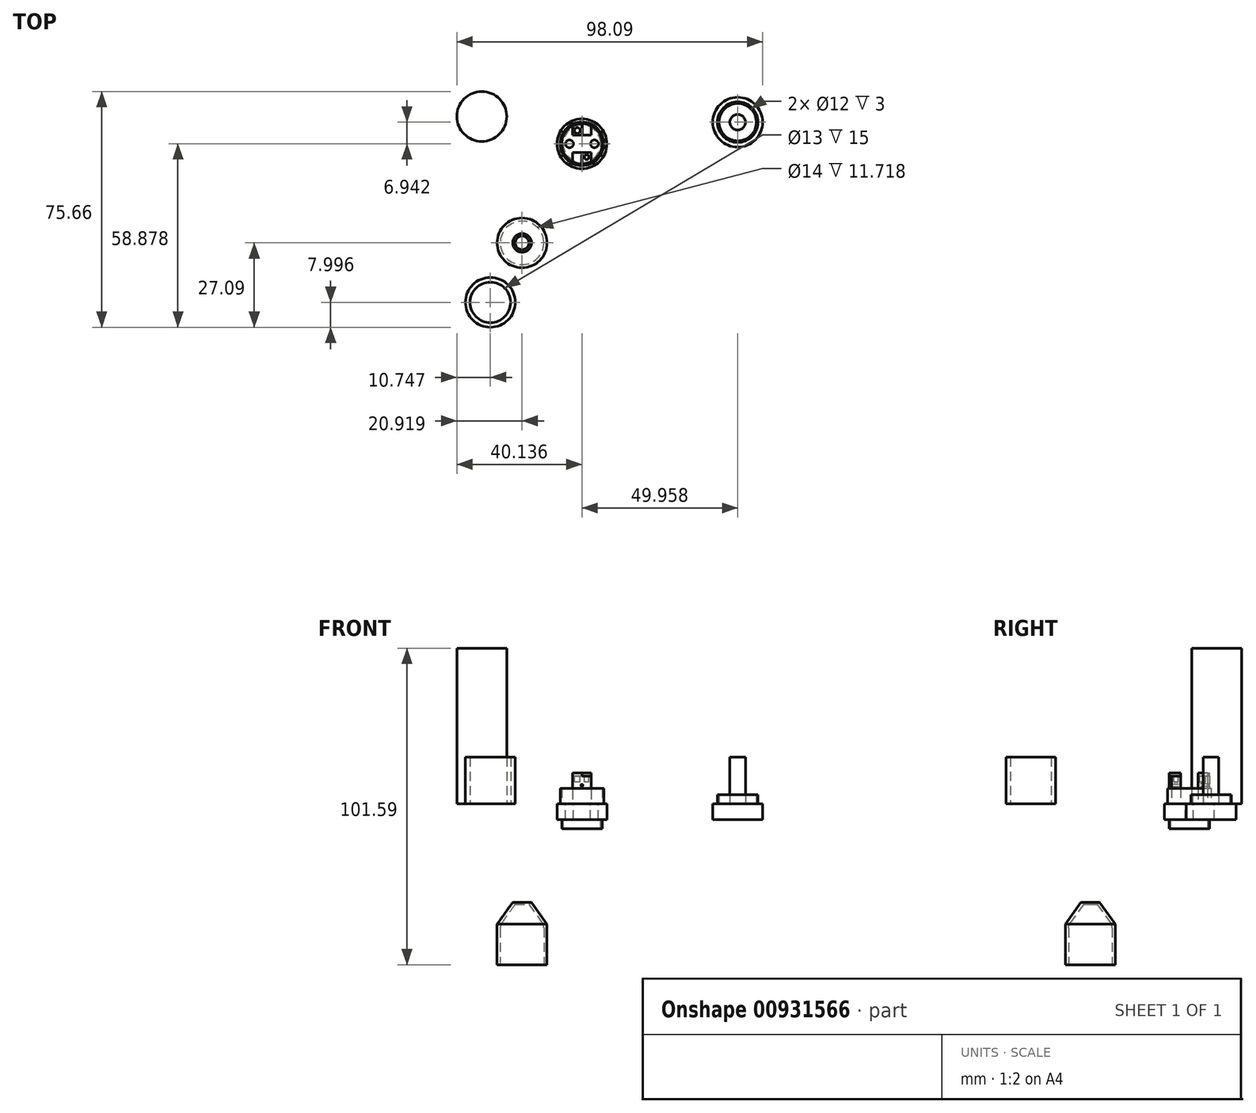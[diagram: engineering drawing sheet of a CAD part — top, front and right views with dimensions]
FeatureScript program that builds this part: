
annotation { "Feature Type Name" : "Feature", "Feature Type Description" : "" }
export const myFeature = defineFeature(function(context is Context, id is Id, definition is map)
    precondition{}
    {
        {
            var Q0;
            Q0=qCreatedBy(makeId("Top.planeOp"),FACE);
            var sketch = newSketch(context, id + "F0", { "sketchPlane" : qUnion([Q0])});
            skCircle(sketch, "E0", {"center": v(-50.1, 40.57) * mm, "radius": 8 * mm});
            skSolve(sketch);
        }
        {
            var Q0;
            Q0=makeQuery(id+"F0.imprint","IMPRINT",FACE,{"disambiguationData":[TD([[makeQuery(id+"F0.imprint","IMPRINT",EDGE,{"derivedFrom":sQuery(id+"F0.wireOp",EDGE,"E0")}),1.0]])]});
            extrude(context, id + "F1", {"entities" : qUnion([Q0]), "depth" : 50 * mm, "offsetDistance" : 25 * mm});
        }
        {
            var Q0;
            Q0=qCreatedBy(makeId("Top.planeOp"),FACE);
            var sketch = newSketch(context, id + "F2", { "sketchPlane" : qUnion([Q0])});
            skCircle(sketch, "E1", {"center": v(-17.96, 31.79) * mm, "radius": 8 * mm});
            skCircle(sketch, "E2.0", {"center": v(-17.96, 31.79) * mm, "radius": 6.5 * mm});
            skCircle(sketch, "E3.0", {"center": v(-17.96, 31.79) * mm, "radius": 7 * mm});
            skCircle(sketch, "E4.0", {"center": v(-17.96, 31.79) * mm, "radius": 6 * mm});
            skLineSegment(sketch, "E5.left", {"start": v(-20.96, 37.55) * mm, "end": v(-20.96, 34.55) * mm});
            skLineSegment(sketch, "E5.right", {"start": v(-14.96, 37.55) * mm, "end": v(-14.96, 34.55) * mm});
            skLineSegment(sketch, "E6", {"start": v(-20.96, 29.02) * mm, "end": v(-14.96, 29.02) * mm});
            skLineSegment(sketch, "E7", {"start": v(-20.96, 34.55) * mm, "end": v(-14.96, 34.55) * mm});
            skLineSegment(sketch, "E8.trimOffspring", {"start": v(-20.96, 29.02) * mm, "end": v(-20.96, 26.02) * mm});
            skLineSegment(sketch, "E9.trimOffspring", {"start": v(-14.96, 29.02) * mm, "end": v(-14.96, 26.02) * mm});
            skPoint(sketch, "E10", {"position": v(-13.96, 31.79) * mm});
            skPoint(sketch, "E11", {"position": v(-21.96, 31.79) * mm});
            skSolve(sketch);
        }
        {
            var Q0;
            Q0=qCreatedBy(makeId("Top.planeOp"),FACE);
            var sketch = newSketch(context, id + "F3", { "sketchPlane" : qUnion([Q0])});
            skCircle(sketch, "E12", {"center": v(32, 38.73) * mm, "radius": 8 * mm});
            skCircle(sketch, "E13.0", {"center": v(32, 38.73) * mm, "radius": 6.5 * mm});
            skCircle(sketch, "E14", {"center": v(32, 38.73) * mm, "radius": 2.5 * mm});
            skCircle(sketch, "E15.0", {"center": v(32, 38.73) * mm, "radius": 6 * mm});
            skPoint(sketch, "E16", {"position": v(-21.96, 31.79) * mm});
            skPoint(sketch, "E17", {"position": v(-13.96, 31.79) * mm});
            skSolve(sketch);
        }
        {
            var Q0;
            Q0=makeQuery(id+"F3.imprint","IMPRINT",FACE,{"disambiguationData":[TD([[makeQuery(id+"F3.imprint","IMPRINT",EDGE,{"derivedFrom":sQuery(id+"F3.wireOp",EDGE,"E14")}),1.0]])]});
            var Q1;
            Q1=makeQuery(id+"F3.imprint","IMPRINT",FACE,{"disambiguationData":[TD([[makeQuery(id+"F3.imprint","IMPRINT",EDGE,{"derivedFrom":sQuery(id+"F3.wireOp",EDGE,"E14")}),-1.0]])]});
            var Q2;
            Q2=makeQuery(id+"F3.imprint","IMPRINT",FACE,{"disambiguationData":[TD([[makeQuery(id+"F3.imprint","IMPRINT",EDGE,{"derivedFrom":sQuery(id+"F3.wireOp",EDGE,"E13.0")}),1.0]])]});
            var Q3;
            Q3=makeQuery(id+"F3.imprint","IMPRINT",FACE,{"disambiguationData":[TD([[makeQuery(id+"F3.imprint","IMPRINT",EDGE,{"derivedFrom":sQuery(id+"F3.wireOp",EDGE,"E12")}),1.0]])]});
            extrude(context, id + "F4", {"entities" : qUnion([Q0, Q1, Q2, Q3]), "oppositeDirection" : true, "depth" : 5 * mm, "offsetDistance" : 25 * mm});
        }
        {
            var Q0;
            Q0=makeQuery(id+"F3.imprint","IMPRINT",FACE,{"disambiguationData":[TD([[makeQuery(id+"F3.imprint","IMPRINT",EDGE,{"derivedFrom":sQuery(id+"F3.wireOp",EDGE,"E13.0")}),1.0]])]});
            extrude(context, id + "F5", {"entities" : qUnion([Q0]), "operationType" : NewBodyOperationType.ADD, "depth" : 3 * mm, "offsetDistance" : 25 * mm});
        }
        {
            var Q0;
            Q0=makeQuery(id+"F3.imprint","IMPRINT",FACE,{"disambiguationData":[TD([[makeQuery(id+"F3.imprint","IMPRINT",EDGE,{"derivedFrom":sQuery(id+"F3.wireOp",EDGE,"E14")}),1.0]])]});
            extrude(context, id + "F6", {"entities" : qUnion([Q0]), "operationType" : NewBodyOperationType.ADD, "depth" : 15 * mm, "offsetDistance" : 25 * mm});
        }
        {
            var Q0;
            {var subQ0=sQuery(id+"F2.wireOp",EDGE,"E8.trimOffspring");var subQ1=sQuery(id+"F2.wireOp",EDGE,"E2.0");var subQ2=makeQuery(id+"F2.imprint","INTERSECT",VERTEX,{"derivedFrom":[subQ1,subQ0]});Q0=makeQuery(id+"F2.imprint","IMPRINT",FACE,{"disambiguationData":[TD([[makeQuery(id+"F2.imprint","IMPRINT",EDGE,{"disambiguationData":[TD([[subQ2,-1.0]])],"derivedFrom":subQ1}),1.0]])]});}
            var Q1;
            {var subQ0=sQuery(id+"F2.wireOp",EDGE,"E5.left");var subQ1=sQuery(id+"F2.wireOp",EDGE,"E2.0");var subQ2=makeQuery(id+"F2.imprint","INTERSECT",VERTEX,{"derivedFrom":[subQ1,subQ0]});Q1=makeQuery(id+"F2.imprint","IMPRINT",FACE,{"disambiguationData":[TD([[makeQuery(id+"F2.imprint","IMPRINT",EDGE,{"disambiguationData":[TD([[subQ2,-1.0]])],"derivedFrom":subQ1}),1.0]])]});}
            var Q2;
            Q2=makeQuery(id+"F2.imprint","IMPRINT",FACE,{"disambiguationData":[TD([[makeQuery(id+"F2.imprint","IMPRINT",EDGE,{"derivedFrom":sQuery(id+"F2.wireOp",EDGE,"E1")}),1.0]])]});
            var Q3;
            {var subQ5=sQuery(id+"F2.wireOp",EDGE,"E7");Q3=makeQuery(id+"F2.imprint","IMPRINT",FACE,{"disambiguationData":[TD([[makeQuery(id+"F2.imprint","IMPRINT",EDGE,{"derivedFrom":subQ5}),1.0]])]});}
            var Q4;
            Q4=makeQuery(id+"F2.imprint","IMPRINT",FACE,{"disambiguationData":[TD([[makeQuery(id+"F2.imprint","IMPRINT",EDGE,{"derivedFrom":sQuery(id+"F2.wireOp",EDGE,"E3.0")}),1.0]])]});
            var Q5;
            {var subQ0=sQuery(id+"F2.wireOp",EDGE,"E5.right");var subQ1=sQuery(id+"F2.wireOp",EDGE,"E2.0");var subQ2=makeQuery(id+"F2.imprint","INTERSECT",VERTEX,{"derivedFrom":[subQ1,subQ0]});Q5=makeQuery(id+"F2.imprint","IMPRINT",FACE,{"disambiguationData":[TD([[makeQuery(id+"F2.imprint","IMPRINT",EDGE,{"disambiguationData":[TD([[subQ2,1.0]])],"derivedFrom":subQ1}),1.0]])]});}
            var Q6;
            {var subQ5=sQuery(id+"F2.wireOp",EDGE,"E6");Q6=makeQuery(id+"F2.imprint","IMPRINT",FACE,{"disambiguationData":[TD([[makeQuery(id+"F2.imprint","IMPRINT",EDGE,{"derivedFrom":subQ5}),-1.0]])]});}
            var Q7;
            {var subQ10=sQuery(id+"F2.wireOp",EDGE,"E6");Q7=makeQuery(id+"F2.imprint","IMPRINT",FACE,{"disambiguationData":[TD([[makeQuery(id+"F2.imprint","IMPRINT",EDGE,{"derivedFrom":subQ10}),1.0]])]});}
            var Q8;
            {var subQ0=sQuery(id+"F2.wireOp",EDGE,"E5.left");var subQ1=sQuery(id+"F2.wireOp",EDGE,"E2.0");var subQ2=makeQuery(id+"F2.imprint","INTERSECT",VERTEX,{"derivedFrom":[subQ1,subQ0]});Q8=makeQuery(id+"F2.imprint","IMPRINT",FACE,{"disambiguationData":[TD([[makeQuery(id+"F2.imprint","IMPRINT",EDGE,{"disambiguationData":[TD([[subQ2,1.0]])],"derivedFrom":subQ1}),1.0]])]});}
            extrude(context, id + "F7", {"entities" : qUnion([Q0, Q1, Q2, Q3, Q4, Q5, Q6, Q7, Q8]), "oppositeDirection" : true, "depth" : 5 * mm, "offsetDistance" : 25 * mm});
        }
        {
            var Q0;
            {var subQ0=sQuery(id+"F2.wireOp",EDGE,"E5.right");var subQ1=sQuery(id+"F2.wireOp",EDGE,"E2.0");var subQ2=makeQuery(id+"F2.imprint","INTERSECT",VERTEX,{"derivedFrom":[subQ1,subQ0]});Q0=makeQuery(id+"F2.imprint","IMPRINT",FACE,{"disambiguationData":[TD([[makeQuery(id+"F2.imprint","IMPRINT",EDGE,{"disambiguationData":[TD([[subQ2,1.0]])],"derivedFrom":subQ1}),1.0]])]});}
            var Q1;
            {var subQ0=sQuery(id+"F2.wireOp",EDGE,"E8.trimOffspring");var subQ1=sQuery(id+"F2.wireOp",EDGE,"E2.0");var subQ2=makeQuery(id+"F2.imprint","INTERSECT",VERTEX,{"derivedFrom":[subQ1,subQ0]});Q1=makeQuery(id+"F2.imprint","IMPRINT",FACE,{"disambiguationData":[TD([[makeQuery(id+"F2.imprint","IMPRINT",EDGE,{"disambiguationData":[TD([[subQ2,-1.0]])],"derivedFrom":subQ1}),1.0]])]});}
            var Q2;
            {var subQ0=sQuery(id+"F2.wireOp",EDGE,"E5.left");var subQ1=sQuery(id+"F2.wireOp",EDGE,"E2.0");var subQ2=makeQuery(id+"F2.imprint","INTERSECT",VERTEX,{"derivedFrom":[subQ1,subQ0]});Q2=makeQuery(id+"F2.imprint","IMPRINT",FACE,{"disambiguationData":[TD([[makeQuery(id+"F2.imprint","IMPRINT",EDGE,{"disambiguationData":[TD([[subQ2,1.0]])],"derivedFrom":subQ1}),1.0]])]});}
            var Q3;
            {var subQ0=sQuery(id+"F2.wireOp",EDGE,"E5.left");var subQ1=sQuery(id+"F2.wireOp",EDGE,"E2.0");var subQ2=makeQuery(id+"F2.imprint","INTERSECT",VERTEX,{"derivedFrom":[subQ1,subQ0]});Q3=makeQuery(id+"F2.imprint","IMPRINT",FACE,{"disambiguationData":[TD([[makeQuery(id+"F2.imprint","IMPRINT",EDGE,{"disambiguationData":[TD([[subQ2,-1.0]])],"derivedFrom":subQ1}),1.0]])]});}
            extrude(context, id + "F8", {"entities" : qUnion([Q0, Q1, Q2, Q3]), "operationType" : NewBodyOperationType.ADD, "oppositeDirection" : true, "depth" : 8 * mm, "offsetDistance" : 25 * mm});
        }
        {
            var Q0;
            Q0=makeQuery(id+"F2.imprint","IMPRINT",FACE,{"disambiguationData":[TD([[makeQuery(id+"F2.imprint","IMPRINT",EDGE,{"derivedFrom":sQuery(id+"F2.wireOp",EDGE,"E3.0")}),1.0]])]});
            extrude(context, id + "F9", {"entities" : qUnion([Q0]), "operationType" : NewBodyOperationType.ADD, "depth" : 5 * mm, "offsetDistance" : 25 * mm});
        }
        {
            var Q0;
            {var subQ10=sQuery(id+"F2.wireOp",EDGE,"E6");Q0=makeQuery(id+"F2.imprint","IMPRINT",FACE,{"disambiguationData":[TD([[makeQuery(id+"F2.imprint","IMPRINT",EDGE,{"derivedFrom":subQ10}),1.0]])]});}
            var sketch = newSketch(context, id + "F10", { "sketchPlane" : qUnion([Q0])});
            skPoint(sketch, "E18", {"position": v(-13.96, 31.79) * mm});
            skPoint(sketch, "E19", {"position": v(-21.96, 31.79) * mm});
            skCircle(sketch, "E20", {"center": v(-21.96, 31.79) * mm, "radius": 1.25 * mm});
            skCircle(sketch, "E21", {"center": v(-13.96, 31.79) * mm, "radius": 1.25 * mm});
            skSolve(sketch);
        }
        {
            var Q0;
            Q0=makeQuery(id+"F10.imprint","IMPRINT",FACE,{"disambiguationData":[TD([[makeQuery(id+"F10.imprint","IMPRINT",EDGE,{"derivedFrom":sQuery(id+"F10.wireOp",EDGE,"E21")}),1.0]])]});
            var Q1;
            Q1=makeQuery(id+"F10.imprint","IMPRINT",FACE,{"disambiguationData":[TD([[makeQuery(id+"F10.imprint","IMPRINT",EDGE,{"derivedFrom":sQuery(id+"F10.wireOp",EDGE,"E20")}),1.0]])]});
            extrude(context, id + "F11", {"entities" : qUnion([Q0, Q1]), "operationType" : NewBodyOperationType.REMOVE, "oppositeDirection" : true, "depth" : 40 * mm, "offsetDistance" : 25 * mm});
        }
        {
            var Q0;
            {var subQ5=sQuery(id+"F2.wireOp",EDGE,"E6");Q0=makeQuery(id+"F2.imprint","IMPRINT",FACE,{"disambiguationData":[TD([[makeQuery(id+"F2.imprint","IMPRINT",EDGE,{"derivedFrom":subQ5}),-1.0]])]});}
            var Q1;
            {var subQ0=sQuery(id+"F2.wireOp",EDGE,"E8.trimOffspring");var subQ1=sQuery(id+"F2.wireOp",EDGE,"E2.0");var subQ2=makeQuery(id+"F2.imprint","INTERSECT",VERTEX,{"derivedFrom":[subQ1,subQ0]});Q1=makeQuery(id+"F2.imprint","IMPRINT",FACE,{"disambiguationData":[TD([[makeQuery(id+"F2.imprint","IMPRINT",EDGE,{"disambiguationData":[TD([[subQ2,-1.0]])],"derivedFrom":subQ1}),1.0]])]});}
            var Q2;
            {var subQ0=sQuery(id+"F2.wireOp",EDGE,"E5.left");var subQ1=sQuery(id+"F2.wireOp",EDGE,"E2.0");var subQ2=makeQuery(id+"F2.imprint","INTERSECT",VERTEX,{"derivedFrom":[subQ1,subQ0]});Q2=makeQuery(id+"F2.imprint","IMPRINT",FACE,{"disambiguationData":[TD([[makeQuery(id+"F2.imprint","IMPRINT",EDGE,{"disambiguationData":[TD([[subQ2,1.0]])],"derivedFrom":subQ1}),1.0]])]});}
            var Q3;
            {var subQ5=sQuery(id+"F2.wireOp",EDGE,"E7");Q3=makeQuery(id+"F2.imprint","IMPRINT",FACE,{"disambiguationData":[TD([[makeQuery(id+"F2.imprint","IMPRINT",EDGE,{"derivedFrom":subQ5}),1.0]])]});}
            extrude(context, id + "F12", {"entities" : qUnion([Q0, Q1, Q2, Q3]), "operationType" : NewBodyOperationType.ADD, "depth" : 10 * mm, "offsetDistance" : 25 * mm});
        }
        {
            var Q0;
            Q0=makeQuery(id+"F12.opExtrude","SWEPT_FACE",FACE,{"disambiguationData":[OSD([sQuery(id+"F2.wireOp",EDGE,"E7")])]});
            var sketch = newSketch(context, id + "F13", { "sketchPlane" : qUnion([Q0])});
            skPoint(sketch, "E22", {"position": v(-17.96, 6) * mm});
            skCircle(sketch, "E23", {"center": v(-17.96, 6) * mm, "radius": 0.35 * mm});
            skSolve(sketch);
        }
        {
            var Q0;
            Q0=makeQuery(id+"F12.opExtrude","SWEPT_FACE",FACE,{"disambiguationData":[OSD([sQuery(id+"F2.wireOp",EDGE,"E6")])]});
            var sketch = newSketch(context, id + "F14", { "sketchPlane" : qUnion([Q0])});
            skPoint(sketch, "E24", {"position": v(17.96, 6) * mm});
            skCircle(sketch, "E25", {"center": v(17.96, 6) * mm, "radius": 0.35 * mm});
            skSolve(sketch);
        }
        {
            var Q0;
            Q0=makeQuery(id+"F13.imprint","IMPRINT",FACE,{"disambiguationData":[TD([[makeQuery(id+"F13.imprint","IMPRINT",EDGE,{"derivedFrom":sQuery(id+"F13.wireOp",EDGE,"E23")}),1.0]])]});
            extrude(context, id + "F15", {"entities" : qUnion([Q0]), "operationType" : NewBodyOperationType.REMOVE, "oppositeDirection" : true, "depth" : 25 * mm, "offsetDistance" : 25 * mm});
        }
        {
            var Q0;
            Q0=makeQuery(id+"F14.imprint","IMPRINT",FACE,{"disambiguationData":[TD([[makeQuery(id+"F14.imprint","IMPRINT",EDGE,{"derivedFrom":sQuery(id+"F14.wireOp",EDGE,"E25")}),1.0]])]});
            extrude(context, id + "F16", {"entities" : qUnion([Q0]), "operationType" : NewBodyOperationType.REMOVE, "oppositeDirection" : true, "depth" : 25 * mm, "offsetDistance" : 25 * mm});
        }
        {
            var Q0;
            Q0=qCreatedBy(makeId("Top.planeOp"),FACE);
            var sketch = newSketch(context, id + "F17", { "sketchPlane" : qUnion([Q0])});
            skCircle(sketch, "E26", {"center": v(-47.35, -19.1) * mm, "radius": 8 * mm});
            skCircle(sketch, "E27.0", {"center": v(-47.35, -19.1) * mm, "radius": 6.5 * mm});
            skSolve(sketch);
        }
        {
            var Q0;
            Q0=makeQuery(id+"F17.imprint","IMPRINT",FACE,{"disambiguationData":[TD([[makeQuery(id+"F17.imprint","IMPRINT",EDGE,{"derivedFrom":sQuery(id+"F17.wireOp",EDGE,"E26")}),1.0]])]});
            extrude(context, id + "F18", {"entities" : qUnion([Q0]), "depth" : 15 * mm, "offsetDistance" : 25 * mm});
        }
        {
            var Q0;
            Q0=qCreatedBy(makeId("Front.planeOp"),FACE);
            var sketch = newSketch(context, id + "F19", { "sketchPlane" : qUnion([Q0])});
            skLineSegment(sketch, "E28.top", {"start": v(-45.18, -51.59) * mm, "end": v(-44.18, -51.59) * mm});
            skLineSegment(sketch, "E28.left", {"start": v(-45.18, -38.59) * mm, "end": v(-45.18, -51.59) * mm});
            skLineSegment(sketch, "E29", {"start": v(-45.18, -51.59) * mm, "end": v(-45.18, -38.59) * mm});
            skLineSegment(sketch, "E30", {"start": v(-45.18, -38.59) * mm, "end": v(-40.18, -31.59) * mm});
            skLineSegment(sketch, "E31.0", {"start": v(-44.18, -38.9) * mm, "end": v(-39.37, -32.17) * mm});
            skLineSegment(sketch, "E31.1", {"start": v(-44.18, -51.59) * mm, "end": v(-44.18, -38.9) * mm});
            skLineSegment(sketch, "E32", {"start": v(-40.18, -31.59) * mm, "end": v(-39.37, -32.17) * mm});
            skLineSegment(sketch, "E33", {"start": v(-37.18, -61.59) * mm, "end": v(-37.18, -31.59) * mm});
            skSolve(sketch);
        }
        {
            var Q0;
            Q0=makeQuery(id+"F19.imprint","IMPRINT",FACE,{"disambiguationData":[TD([[makeQuery(id+"F19.imprint","IMPRINT",EDGE,{"derivedFrom":sQuery(id+"F19.wireOp",EDGE,"E28.top")}),1.0]])]});
            var Q1;
            Q1=sQuery(id+"F19.wireOp",EDGE,"E33");
            revolve(context, id + "F20", {"surfaceOperationType" : NewSurfaceOperationType.NEW, "entities" : qUnion([Q0]), "axis" : qUnion([Q1]), "revolveType" : RevolveType.FULL});
        }
        {
            var Q0;
            Q0=makeQuery(id+"F20.opRevolve","SWEPT_EDGE",EDGE,{"disambiguationData":[OSD([sQuery(id+"F19.wireOp",EDGE,"E31.0"),sQuery(id+"F19.wireOp",EDGE,"E31.1")])]});
            fillet(context, id + "F21", {"entities" : qUnion([Q0]), "radius" : 3 * mm, "tangentPropagation" : true, "allowEdgeOverflow" : false});
        }
        {
            var Q0;
            Q0=makeQuery(id+"F12.opExtrude","CAP_FACE",FACE,{"disambiguationData":[OSD([sQuery(id+"F2.wireOp",EDGE,"E2.0"),sQuery(id+"F2.wireOp",EDGE,"E5.left"),sQuery(id+"F2.wireOp",EDGE,"E5.right"),sQuery(id+"F2.wireOp",EDGE,"E7")])],"isStart":false});
            var sketch = newSketch(context, id + "F22", { "sketchPlane" : qUnion([Q0])});
            skLineSegment(sketch, "E34.bottom", {"start": v(-20.96, 34.55) * mm, "end": v(-17.96, 34.55) * mm});
            skLineSegment(sketch, "E34.top", {"start": v(-20.96, 37.55) * mm, "end": v(-17.96, 37.55) * mm});
            skLineSegment(sketch, "E34.left", {"start": v(-20.96, 34.55) * mm, "end": v(-20.96, 37.55) * mm});
            skLineSegment(sketch, "E34.right", {"start": v(-17.96, 34.55) * mm, "end": v(-17.96, 37.55) * mm});
            skPoint(sketch, "E35", {"position": v(-19.46, 36.05) * mm});
            skCircle(sketch, "E36", {"center": v(-19.46, 36.05) * mm, "radius": 0.92 * mm});
            skSolve(sketch);
        }
        {
            var Q0;
            Q0=makeQuery(id+"F22.imprint","IMPRINT",FACE,{"disambiguationData":[TD([[makeQuery(id+"F22.imprint","IMPRINT",EDGE,{"derivedFrom":sQuery(id+"F22.wireOp",EDGE,"E36")}),1.0]])]});
            var Q1;
            Q1=makeQuery(id+"F22.imprint","IMPRINT",FACE,{"disambiguationData":[TD([[makeQuery(id+"F22.imprint","IMPRINT",EDGE,{"derivedFrom":sQuery(id+"F22.wireOp",EDGE,"E34.bottom")}),1.0]])]});
            extrude(context, id + "F23", {"entities" : qUnion([Q0, Q1]), "operationType" : NewBodyOperationType.REMOVE, "oppositeDirection" : true, "depth" : 1 * mm, "offsetDistance" : 25 * mm});
        }
        {
            var Q0;
            Q0=makeQuery(id+"F22.imprint","IMPRINT",FACE,{"disambiguationData":[TD([[makeQuery(id+"F22.imprint","IMPRINT",EDGE,{"derivedFrom":sQuery(id+"F22.wireOp",EDGE,"E36")}),1.0]])]});
            extrude(context, id + "F24", {"entities" : qUnion([Q0]), "operationType" : NewBodyOperationType.REMOVE, "oppositeDirection" : true, "depth" : 3 * mm, "offsetDistance" : 25 * mm});
        }
        {
            var Q0;
            Q0=makeQuery(id+"F12.opExtrude","CAP_FACE",FACE,{"disambiguationData":[OSD([sQuery(id+"F2.wireOp",EDGE,"E2.0"),sQuery(id+"F2.wireOp",EDGE,"E6"),sQuery(id+"F2.wireOp",EDGE,"E8.trimOffspring"),sQuery(id+"F2.wireOp",EDGE,"E9.trimOffspring")])],"isStart":false});
            var sketch = newSketch(context, id + "F25", { "sketchPlane" : qUnion([Q0])});
            skLineSegment(sketch, "E37.bottom", {"start": v(-14.96, 29.02) * mm, "end": v(-17.96, 29.02) * mm});
            skLineSegment(sketch, "E37.top", {"start": v(-14.96, 26.02) * mm, "end": v(-17.96, 26.02) * mm});
            skLineSegment(sketch, "E37.left", {"start": v(-14.96, 29.02) * mm, "end": v(-14.96, 26.02) * mm});
            skLineSegment(sketch, "E37.right", {"start": v(-17.96, 29.02) * mm, "end": v(-17.96, 26.02) * mm});
            skPoint(sketch, "E38", {"position": v(-16.46, 27.52) * mm});
            skPoint(sketch, "E38.positionSnap0", {"position": v(-16.46, 29.02) * mm});
            skCircle(sketch, "E39", {"center": v(-16.46, 27.52) * mm, "radius": 0.75 * mm});
            skSolve(sketch);
        }
        {
            var Q0;
            Q0=makeQuery(id+"F25.imprint","IMPRINT",FACE,{"disambiguationData":[TD([[makeQuery(id+"F25.imprint","IMPRINT",EDGE,{"derivedFrom":sQuery(id+"F25.wireOp",EDGE,"E39")}),1.0]])]});
            var Q1;
            Q1=makeQuery(id+"F25.imprint","IMPRINT",FACE,{"disambiguationData":[TD([[makeQuery(id+"F25.imprint","IMPRINT",EDGE,{"derivedFrom":sQuery(id+"F25.wireOp",EDGE,"E37.bottom")}),-1.0]])]});
            extrude(context, id + "F26", {"entities" : qUnion([Q0, Q1]), "operationType" : NewBodyOperationType.REMOVE, "oppositeDirection" : true, "depth" : 1 * mm, "offsetDistance" : 25 * mm});
        }
        {
            var Q0;
            Q0=makeQuery(id+"F25.imprint","IMPRINT",FACE,{"disambiguationData":[TD([[makeQuery(id+"F25.imprint","IMPRINT",EDGE,{"derivedFrom":sQuery(id+"F25.wireOp",EDGE,"E39")}),1.0]])]});
            extrude(context, id + "F27", {"entities" : qUnion([Q0]), "operationType" : NewBodyOperationType.REMOVE, "oppositeDirection" : true, "depth" : 3 * mm, "offsetDistance" : 25 * mm});
        }
        {
            var Q0;
            Q0=makeQuery(id+"F12.opExtrude","CAP_FACE",FACE,{"disambiguationData":[OSD([sQuery(id+"F2.wireOp",EDGE,"E2.0"),sQuery(id+"F2.wireOp",EDGE,"E5.left"),sQuery(id+"F2.wireOp",EDGE,"E5.right"),sQuery(id+"F2.wireOp",EDGE,"E7")])],"isStart":false});
            var sketch = newSketch(context, id + "F28", { "sketchPlane" : qUnion([Q0])});
            skLineSegment(sketch, "E40", {"start": v(-17.96, 37.55) * mm, "end": v(-17.96, 38.29) * mm});
            skSolve(sketch);
        }
        {
            var Q0;
            {var subQ0=sQuery(id+"F28.wireOp",EDGE,"E40");Q0=makeQuery(id+"F28.imprint","IMPRINT",FACE,{"disambiguationData":[TD([[makeQuery(id+"F28.imprint","IMPRINT",EDGE,{"derivedFrom":subQ0}),1.0]])]});}
            extrude(context, id + "F29", {"entities" : qUnion([Q0]), "operationType" : NewBodyOperationType.REMOVE, "oppositeDirection" : true, "depth" : 1 * mm, "offsetDistance" : 25 * mm});
        }
        {
            var Q0;
            Q0=makeQuery(id+"F12.opExtrude","CAP_FACE",FACE,{"disambiguationData":[OSD([sQuery(id+"F2.wireOp",EDGE,"E2.0"),sQuery(id+"F2.wireOp",EDGE,"E6"),sQuery(id+"F2.wireOp",EDGE,"E8.trimOffspring"),sQuery(id+"F2.wireOp",EDGE,"E9.trimOffspring")])],"isStart":false});
            var sketch = newSketch(context, id + "F30", { "sketchPlane" : qUnion([Q0])});
            skLineSegment(sketch, "E41", {"start": v(-17.96, 26.02) * mm, "end": v(-17.96, 25.29) * mm});
            skSolve(sketch);
        }
        {
            var Q0;
            {var subQ0=sQuery(id+"F30.wireOp",EDGE,"E41");Q0=makeQuery(id+"F30.imprint","IMPRINT",FACE,{"disambiguationData":[TD([[makeQuery(id+"F30.imprint","IMPRINT",EDGE,{"derivedFrom":subQ0}),1.0]])]});}
            extrude(context, id + "F31", {"entities" : qUnion([Q0]), "operationType" : NewBodyOperationType.REMOVE, "oppositeDirection" : true, "depth" : 1 * mm, "offsetDistance" : 25 * mm});
        }
    });
